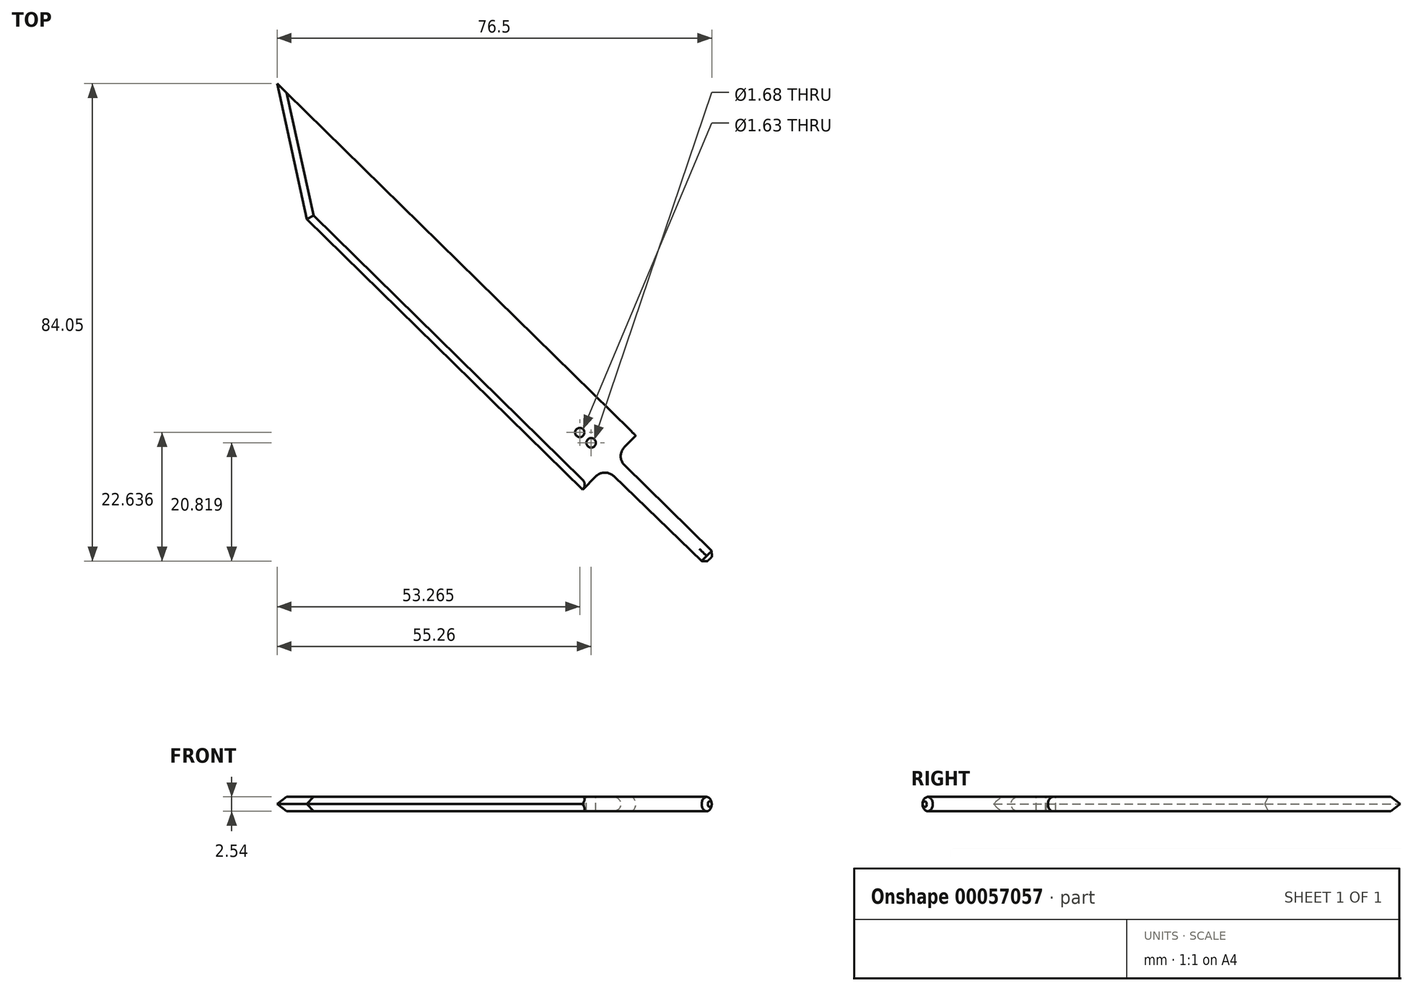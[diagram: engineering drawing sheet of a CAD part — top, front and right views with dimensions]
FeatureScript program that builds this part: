
annotation { "Feature Type Name" : "Feature", "Feature Type Description" : "" }
export const myFeature = defineFeature(function(context is Context, id is Id, definition is map)
    precondition{}
    {
        {
            var Q0;
            Q0=qCreatedBy(makeId("Top.planeOp"),FACE);
            var sketch = newSketch(context, id + "F0", { "sketchPlane" : qUnion([Q0])});
            skLineSegment(sketch, "E0", {"start": v(-77.02, 84.57) * mm, "end": v(-71.79, 60.72) * mm});
            skLineSegment(sketch, "E1", {"start": v(-71.79, 60.72) * mm, "end": v(-23.26, 13.07) * mm});
            skLineSegment(sketch, "E2", {"start": v(-23.26, 13.07) * mm, "end": v(-13.9, 22.6) * mm});
            skLineSegment(sketch, "E3", {"start": v(-13.9, 22.6) * mm, "end": v(-77.02, 84.57) * mm});
            skLineSegment(sketch, "E4", {"start": v(-1.76, 0) * mm, "end": v(0, 1.8) * mm});
            skLineSegment(sketch, "E5", {"start": v(0, 1.8) * mm, "end": v(-17.48, 18.95) * mm});
            skLineSegment(sketch, "E6", {"start": v(-19.4, 17) * mm, "end": v(-1.76, 0) * mm});
            skSolve(sketch);
        }
        {
            var Q0;
            Q0 = qSketchRegion(id + "F0", true);
            extrude(context, id + "F1", {"entities" : qUnion([Q0]), "depth" : 2.54 * mm});
        }
        {
            var Q0;
            Q0=makeQuery(id+"F1.opExtrude","CAP_FACE",FACE,{"disambiguationData":[OSD([sQuery(id+"F0.wireOp",EDGE,"E0"),sQuery(id+"F0.wireOp",EDGE,"E1"),sQuery(id+"F0.wireOp",EDGE,"E2"),sQuery(id+"F0.wireOp",EDGE,"E3"),sQuery(id+"F0.wireOp",EDGE,"E4"),sQuery(id+"F0.wireOp",EDGE,"E5"),sQuery(id+"F0.wireOp",EDGE,"E6")])],"isStart":false});
            var sketch = newSketch(context, id + "F2", { "sketchPlane" : qUnion([Q0])});
            skCircle(sketch, "E7", {"center": v(-23.76, 23.16) * mm, "radius": 0.82 * mm});
            skCircle(sketch, "E8", {"center": v(-21.76, 21.34) * mm, "radius": 0.84 * mm});
            skSolve(sketch);
        }
        {
            var Q0;
            Q0 = qSketchRegion(id + "F2", true);
            extrude(context, id + "F3", {"entities" : qUnion([Q0]), "operationType" : NewBodyOperationType.REMOVE, "oppositeDirection" : true, "depth" : 25.4 * mm});
        }
        {
            var Q0;
            Q0=makeQuery(id+"F1.opExtrude","CAP_EDGE",EDGE,{"disambiguationData":[OSD([sQuery(id+"F0.wireOp",EDGE,"E1")])],"isStart":false});
            var Q1;
            Q1=makeQuery(id+"F1.opExtrude","CAP_EDGE",EDGE,{"disambiguationData":[OSD([sQuery(id+"F0.wireOp",EDGE,"E1")])],"isStart":true});
            var Q2;
            Q2=makeQuery(id+"F1.opExtrude","CAP_EDGE",EDGE,{"disambiguationData":[OSD([sQuery(id+"F0.wireOp",EDGE,"E0")])],"isStart":false});
            var Q3;
            Q3=makeQuery(id+"F1.opExtrude","CAP_EDGE",EDGE,{"disambiguationData":[OSD([sQuery(id+"F0.wireOp",EDGE,"E0")])],"isStart":true});
            chamfer(context, id + "F4", {"entities" : qUnion([Q0, Q1, Q2, Q3]), "width" : 1.27 * mm, "tangentPropagation" : true});
        }
        {
            var Q0;
            Q0=makeQuery(id+"F1.opExtrude","SWEPT_EDGE",EDGE,{"disambiguationData":[OSD([sQuery(id+"F0.wireOp",EDGE,"E2"),sQuery(id+"F0.wireOp",EDGE,"E6")])]});
            var Q1;
            Q1=makeQuery(id+"F1.opExtrude","SWEPT_EDGE",EDGE,{"disambiguationData":[OSD([sQuery(id+"F0.wireOp",EDGE,"E2"),sQuery(id+"F0.wireOp",EDGE,"E5")])]});
            fillet(context, id + "F5", {"entities" : qUnion([Q0, Q1]), "radius" : 2.23 * mm, "tangentPropagation" : true, "allowEdgeOverflow" : false});
        }
        {
            var Q0;
            Q0=makeQuery(id+"F1.opExtrude","CAP_EDGE",EDGE,{"disambiguationData":[OSD([sQuery(id+"F0.wireOp",EDGE,"E5")])],"isStart":false});
            var Q1;
            Q1=makeQuery(id+"F1.opExtrude","CAP_EDGE",EDGE,{"disambiguationData":[OSD([sQuery(id+"F0.wireOp",EDGE,"E6")])],"isStart":false});
            var Q2;
            Q2=makeQuery(id+"F1.opExtrude","CAP_EDGE",EDGE,{"disambiguationData":[OSD([sQuery(id+"F0.wireOp",EDGE,"E5")])],"isStart":true});
            var Q3;
            Q3=makeQuery(id+"F1.opExtrude","CAP_EDGE",EDGE,{"disambiguationData":[OSD([sQuery(id+"F0.wireOp",EDGE,"E6")])],"isStart":true});
            fillet(context, id + "F6", {"entities" : qUnion([Q0, Q1, Q2, Q3]), "radius" : 1.27 * mm, "tangentPropagation" : true, "allowEdgeOverflow" : false});
        }
        {
            var Q0;
            Q0=makeQuery(id+"F6.opFillet","BLEND_EDGE",EDGE,{"blendedFrom":[makeQuery(id+"F1.opExtrude","CAP_EDGE",EDGE,{"disambiguationData":[OSD([sQuery(id+"F0.wireOp",EDGE,"E6")])],"isStart":true}),makeQuery(id+"F1.opExtrude","SWEPT_FACE",FACE,{"disambiguationData":[OSD([sQuery(id+"F0.wireOp",EDGE,"E4")])]})],"blendedInto":[makeQuery(id+"F1.opExtrude","SWEPT_FACE",FACE,{"disambiguationData":[OSD([sQuery(id+"F0.wireOp",EDGE,"E4")])]})]});
            var Q1;
            Q1=makeQuery(id+"F6.opFillet","BLEND_EDGE",EDGE,{"blendedFrom":[makeQuery(id+"F1.opExtrude","CAP_EDGE",EDGE,{"disambiguationData":[OSD([sQuery(id+"F0.wireOp",EDGE,"E5")])],"isStart":false}),makeQuery(id+"F1.opExtrude","SWEPT_FACE",FACE,{"disambiguationData":[OSD([sQuery(id+"F0.wireOp",EDGE,"E4")])]})],"blendedInto":[makeQuery(id+"F1.opExtrude","SWEPT_FACE",FACE,{"disambiguationData":[OSD([sQuery(id+"F0.wireOp",EDGE,"E4")])]})]});
            chamfer(context, id + "F7", {"entities" : qUnion([Q0, Q1]), "width" : 0.76 * mm, "tangentPropagation" : true});
        }
    });
